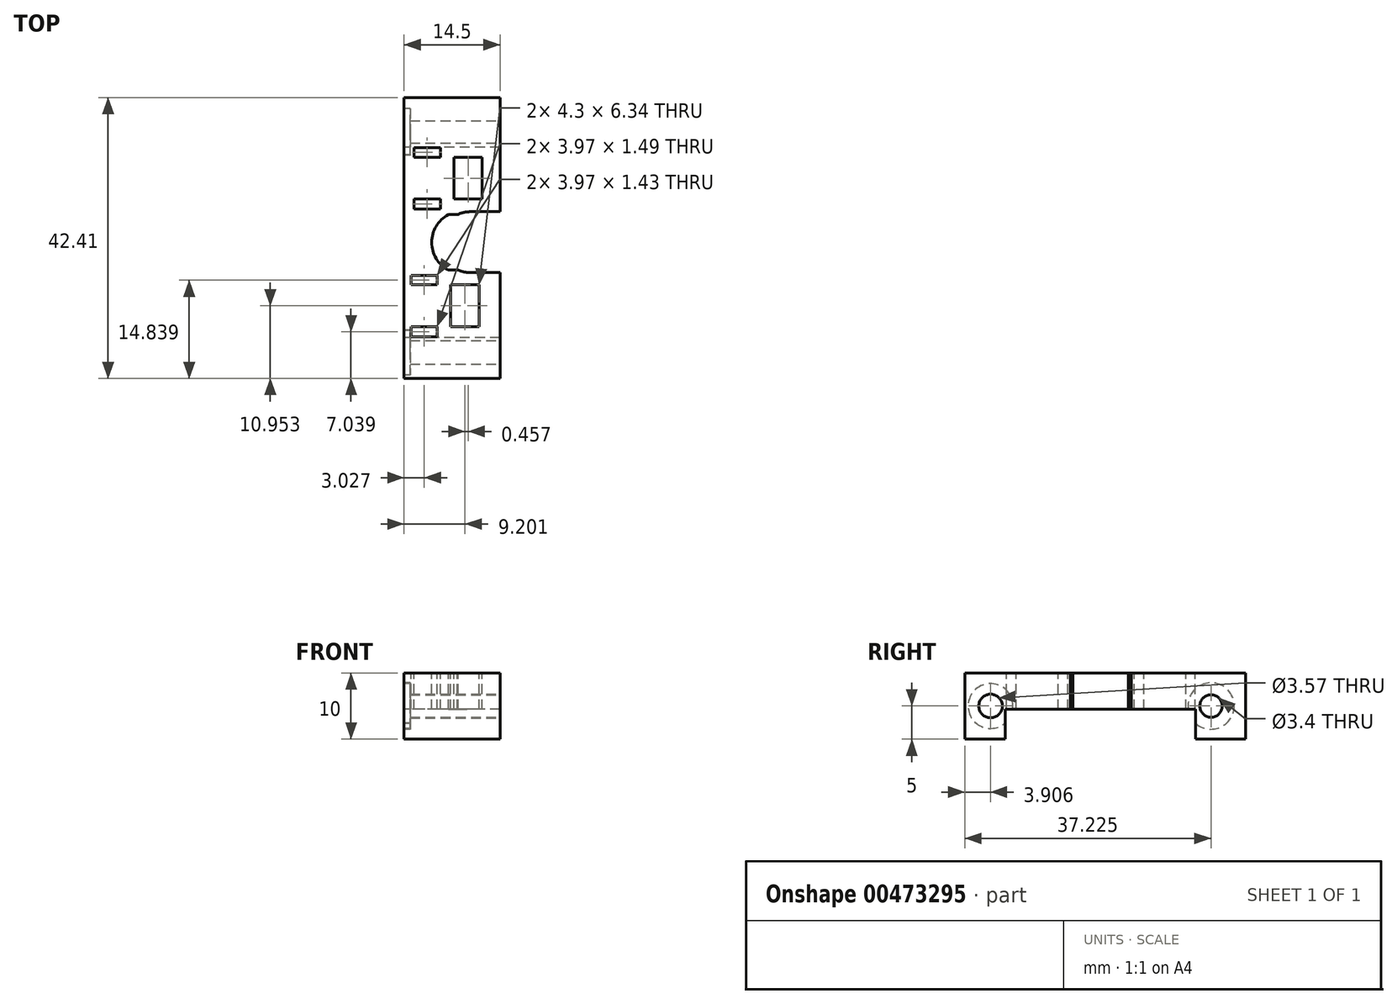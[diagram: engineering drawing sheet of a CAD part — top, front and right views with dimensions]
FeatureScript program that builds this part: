
annotation { "Feature Type Name" : "Feature", "Feature Type Description" : "" }
export const myFeature = defineFeature(function(context is Context, id is Id, definition is map)
    precondition{}
    {
        {
            var Q0;
            Q0=qCreatedBy(makeId("Top.planeOp"),FACE);
            var sketch = newSketch(context, id + "F0", { "sketchPlane" : qUnion([Q0])});
            skLineSegment(sketch, "E0.bottom", {"start": v(8.3, 21.21) * mm, "end": v(-6.2, 21.21) * mm});
            skLineSegment(sketch, "E0.top", {"start": v(8.3, -21.2) * mm, "end": v(-6.2, -21.2) * mm});
            skLineSegment(sketch, "E0.left", {"start": v(8.3, 21.21) * mm, "end": v(8.3, -21.2) * mm});
            skLineSegment(sketch, "E0.right", {"start": v(-6.2, 21.21) * mm, "end": v(-6.2, 5.08) * mm});
            skPoint(sketch, "E1", {"position": v(-1.7, 3.88) * mm});
            skPoint(sketch, "E2", {"position": v(-1.7, -5.12) * mm});
            skLineSegment(sketch, "E3.trimOffspring", {"start": v(-6.2, -6.32) * mm, "end": v(-6.2, -21.2) * mm});
            skCircle(sketch, "E4.0", {"center": v(5.4, -9.25) * mm, "radius": 1.75 * mm});
            skLineSegment(sketch, "E5.0", {"start": v(-1.7, 5.08) * mm, "end": v(-6.2, 5.08) * mm});
            skArc(sketch, "E5.1", {"start": v(-1.7, -6.32) * mm, "mid": v(4, -0.62) * mm, "end": v(-1.7, 5.08) * mm});
            skLineSegment(sketch, "E5.2", {"start": v(-1.7, -6.32) * mm, "end": v(-6.2, -6.32) * mm});
            skSolve(sketch);
        }
        {
            var Q0;
            Q0 = qSketchRegion(id + "F0", true);
            extrude(context, id + "F1", {"entities" : qUnion([Q0]), "depth" : 10 * mm, "offsetDistance" : 25 * mm});
        }
        {
            var Q0;
            Q0=makeQuery(id+"F1.opExtrude","SWEPT_FACE",FACE,{"disambiguationData":[OSD([sQuery(id+"F0.wireOp",EDGE,"E0.left")])]});
            var sketch = newSketch(context, id + "F2", { "sketchPlane" : qUnion([Q0])});
            skCircle(sketch, "E6.0", {"center": v(-17.3, 5) * mm, "radius": 1.78 * mm});
            skCircle(sketch, "E7.0", {"center": v(16.03, 5) * mm, "radius": 1.7 * mm});
            skPoint(sketch, "E8", {"position": v(-21.2, 5) * mm});
            skSolve(sketch);
        }
        {
            var Q0;
            Q0 = qSketchRegion(id + "F2", true);
            extrude(context, id + "F3", {"entities" : qUnion([Q0]), "operationType" : NewBodyOperationType.REMOVE, "oppositeDirection" : true, "depth" : 25 * mm, "offsetDistance" : 25 * mm});
        }
        {
            var Q0;
            Q0=makeQuery(id+"F1.opExtrude","SWEPT_BODY",BODY,{"disambiguationData":[OSD([sQuery(id+"F0.wireOp",EDGE,"E0.bottom"),sQuery(id+"F0.wireOp",EDGE,"E0.top"),sQuery(id+"F0.wireOp",EDGE,"E0.left"),sQuery(id+"F0.wireOp",EDGE,"E0.right"),sQuery(id+"F0.wireOp",EDGE,"E3.trimOffspring"),sQuery(id+"F0.wireOp",EDGE,"E4.0"),sQuery(id+"F0.wireOp",EDGE,"E5.0"),sQuery(id+"F0.wireOp",EDGE,"E5.1"),sQuery(id+"F0.wireOp",EDGE,"E5.2")])]});
            var Q1;
            Q1=makeQuery(id+"F1.opExtrude","SWEPT_FACE",FACE,{"disambiguationData":[OSD([sQuery(id+"F0.wireOp",EDGE,"E0.right")])]});
            mirror(context, id + "F4", {"operationType" : NewBodyOperationType.ADD, "entities" : qUnion([Q0]), "mirrorPlane" : qUnion([Q1])});
        }
        {
            var Q0;
            {var subQ0=makeQuery(id+"F1.opExtrude","CAP_FACE",FACE,{"disambiguationData":[OSD([sQuery(id+"F0.wireOp",EDGE,"E0.bottom"),sQuery(id+"F0.wireOp",EDGE,"E0.top"),sQuery(id+"F0.wireOp",EDGE,"E0.left"),sQuery(id+"F0.wireOp",EDGE,"E0.right"),sQuery(id+"F0.wireOp",EDGE,"E3.trimOffspring"),sQuery(id+"F0.wireOp",EDGE,"E4.0"),sQuery(id+"F0.wireOp",EDGE,"E5.0"),sQuery(id+"F0.wireOp",EDGE,"E5.1"),sQuery(id+"F0.wireOp",EDGE,"E5.2")])],"isStart":false});Q0=makeQuery(id+"F4.boolean.opBoolean","MERGE",FACE,{"derivedFrom":[subQ0,makeQuery(id+"F4.opPattern","COPY",FACE,{"derivedFrom":subQ0,"instanceName":"1"})]});}
            var sketch = newSketch(context, id + "F5", { "sketchPlane" : qUnion([Q0])});
            skLineSegment(sketch, "E9.bottom", {"start": v(-6.2, -21.2) * mm, "end": v(17.5, -21.2) * mm});
            skLineSegment(sketch, "E9.top", {"start": v(-6.2, 26.64) * mm, "end": v(17.5, 26.64) * mm});
            skLineSegment(sketch, "E9.left", {"start": v(-6.2, -21.2) * mm, "end": v(-6.2, 26.64) * mm});
            skLineSegment(sketch, "E9.right", {"start": v(17.5, -21.2) * mm, "end": v(17.5, 26.64) * mm});
            skSolve(sketch);
        }
        {
            var Q0;
            Q0 = qSketchRegion(id + "F5", true);
            extrude(context, id + "F6", {"entities" : qUnion([Q0]), "operationType" : NewBodyOperationType.REMOVE, "oppositeDirection" : true, "depth" : 25 * mm, "offsetDistance" : 25 * mm});
        }
        {
            var Q0;
            {var subQ0=makeQuery(id+"F1.opExtrude","CAP_FACE",FACE,{"disambiguationData":[OSD([sQuery(id+"F0.wireOp",EDGE,"E0.bottom"),sQuery(id+"F0.wireOp",EDGE,"E0.top"),sQuery(id+"F0.wireOp",EDGE,"E0.left"),sQuery(id+"F0.wireOp",EDGE,"E0.right"),sQuery(id+"F0.wireOp",EDGE,"E3.trimOffspring"),sQuery(id+"F0.wireOp",EDGE,"E4.0"),sQuery(id+"F0.wireOp",EDGE,"E5.0"),sQuery(id+"F0.wireOp",EDGE,"E5.1"),sQuery(id+"F0.wireOp",EDGE,"E5.2")])],"isStart":false});Q0=makeQuery(id+"F4.boolean.opBoolean","MERGE",FACE,{"derivedFrom":[subQ0,makeQuery(id+"F4.opPattern","COPY",FACE,{"derivedFrom":subQ0,"instanceName":"1"})]});}
            var sketch = newSketch(context, id + "F7", { "sketchPlane" : qUnion([Q0])});
            skCircle(sketch, "E10.0", {"center": v(-17.8, -9.25) * mm, "radius": 1.75 * mm});
            skSolve(sketch);
        }
        {
            var Q0;
            Q0 = qSketchRegion(id + "F7", true);
            var Q1;
            {var subQ0=makeQuery(id+"F1.opExtrude","CAP_FACE",FACE,{"disambiguationData":[OSD([sQuery(id+"F0.wireOp",EDGE,"E0.bottom"),sQuery(id+"F0.wireOp",EDGE,"E0.top"),sQuery(id+"F0.wireOp",EDGE,"E0.left"),sQuery(id+"F0.wireOp",EDGE,"E0.right"),sQuery(id+"F0.wireOp",EDGE,"E3.trimOffspring"),sQuery(id+"F0.wireOp",EDGE,"E4.0"),sQuery(id+"F0.wireOp",EDGE,"E5.0"),sQuery(id+"F0.wireOp",EDGE,"E5.1"),sQuery(id+"F0.wireOp",EDGE,"E5.2")])],"isStart":true});Q1=makeQuery(id+"F4.boolean.opBoolean","MERGE",FACE,{"derivedFrom":[subQ0,makeQuery(id+"F4.opPattern","COPY",FACE,{"derivedFrom":subQ0,"instanceName":"1"})]});}
            extrude(context, id + "F8", {"entities" : qUnion([Q0]), "operationType" : NewBodyOperationType.ADD, "endBound" : BoundingType.UP_TO_SURFACE, "oppositeDirection" : true, "depth" : 25 * mm, "endBoundEntityFace" : qUnion([Q1]), "offsetDistance" : 25 * mm});
        }
        {
            var Q0;
            {var subQ0=makeQuery(id+"F1.opExtrude","CAP_FACE",FACE,{"disambiguationData":[OSD([sQuery(id+"F0.wireOp",EDGE,"E0.bottom"),sQuery(id+"F0.wireOp",EDGE,"E0.top"),sQuery(id+"F0.wireOp",EDGE,"E0.left"),sQuery(id+"F0.wireOp",EDGE,"E0.right"),sQuery(id+"F0.wireOp",EDGE,"E3.trimOffspring"),sQuery(id+"F0.wireOp",EDGE,"E4.0"),sQuery(id+"F0.wireOp",EDGE,"E5.0"),sQuery(id+"F0.wireOp",EDGE,"E5.1"),sQuery(id+"F0.wireOp",EDGE,"E5.2")])],"isStart":false});Q0=makeQuery(id+"F8.boolean.opBoolean","MERGE",FACE,{"derivedFrom":[makeQuery(id+"F4.boolean.opBoolean","MERGE",FACE,{"derivedFrom":[subQ0,makeQuery(id+"F4.opPattern","COPY",FACE,{"derivedFrom":subQ0,"instanceName":"1"})]}),makeQuery(id+"F8.opExtrude","CAP_FACE",FACE,{"disambiguationData":[OSD([sQuery(id+"F7.wireOp",EDGE,"E10.0")])],"isStart":true})]});}
            var sketch = newSketch(context, id + "F9", { "sketchPlane" : qUnion([Q0])});
            skLineSegment(sketch, "E11", {"start": v(-20.7, 0) * mm, "end": v(-3.31, 0) * mm, "construction": true});
            skLineSegment(sketch, "E12.bottom", {"start": v(-9.35, -7.08) * mm, "end": v(-13.65, -7.08) * mm});
            skLineSegment(sketch, "E12.top", {"start": v(-9.35, -13.42) * mm, "end": v(-13.65, -13.42) * mm});
            skLineSegment(sketch, "E12.left", {"start": v(-9.35, -7.08) * mm, "end": v(-9.35, -13.42) * mm});
            skLineSegment(sketch, "E12.right", {"start": v(-13.65, -7.08) * mm, "end": v(-13.65, -13.42) * mm});
            skLineSegment(sketch, "E13.bottom", {"start": v(-15.69, -7.08) * mm, "end": v(-19.66, -7.08) * mm});
            skLineSegment(sketch, "E13.top", {"start": v(-15.69, -5.64) * mm, "end": v(-19.66, -5.64) * mm});
            skLineSegment(sketch, "E13.left", {"start": v(-15.69, -7.08) * mm, "end": v(-15.69, -5.64) * mm});
            skLineSegment(sketch, "E13.right", {"start": v(-19.66, -7.08) * mm, "end": v(-19.66, -5.64) * mm});
            skLineSegment(sketch, "E14.bottom", {"start": v(-15.69, -13.42) * mm, "end": v(-19.66, -13.42) * mm});
            skLineSegment(sketch, "E14.top", {"start": v(-15.69, -14.9) * mm, "end": v(-19.66, -14.9) * mm});
            skLineSegment(sketch, "E14.left", {"start": v(-15.69, -13.42) * mm, "end": v(-15.69, -14.9) * mm});
            skLineSegment(sketch, "E14.right", {"start": v(-19.66, -13.42) * mm, "end": v(-19.66, -14.9) * mm});
            skLineSegment(sketch, "E15.bottom", {"start": v(-8.9, 12.22) * mm, "end": v(-13.2, 12.22) * mm});
            skLineSegment(sketch, "E15.top", {"start": v(-8.9, 5.88) * mm, "end": v(-13.2, 5.88) * mm});
            skLineSegment(sketch, "E15.left", {"start": v(-8.9, 12.22) * mm, "end": v(-8.9, 5.88) * mm});
            skLineSegment(sketch, "E15.right", {"start": v(-13.2, 12.22) * mm, "end": v(-13.2, 5.88) * mm});
            skLineSegment(sketch, "E16.bottom", {"start": v(-15.23, 12.22) * mm, "end": v(-19.2, 12.22) * mm});
            skLineSegment(sketch, "E16.top", {"start": v(-15.23, 13.65) * mm, "end": v(-19.2, 13.65) * mm});
            skLineSegment(sketch, "E16.left", {"start": v(-15.23, 12.22) * mm, "end": v(-15.23, 13.65) * mm});
            skLineSegment(sketch, "E16.right", {"start": v(-19.2, 12.22) * mm, "end": v(-19.2, 13.65) * mm});
            skLineSegment(sketch, "E17.bottom", {"start": v(-15.23, 5.88) * mm, "end": v(-19.2, 5.88) * mm});
            skLineSegment(sketch, "E17.top", {"start": v(-15.23, 4.4) * mm, "end": v(-19.2, 4.4) * mm});
            skLineSegment(sketch, "E17.left", {"start": v(-15.23, 5.88) * mm, "end": v(-15.23, 4.4) * mm});
            skLineSegment(sketch, "E17.right", {"start": v(-19.2, 5.88) * mm, "end": v(-19.2, 4.4) * mm});
            skSolve(sketch);
        }
        {
            var Q0;
            Q0 = qSketchRegion(id + "F9", true);
            extrude(context, id + "F10", {"entities" : qUnion([Q0]), "operationType" : NewBodyOperationType.REMOVE, "oppositeDirection" : true, "depth" : 25 * mm, "offsetDistance" : 25 * mm});
        }
        {
            var Q0;
            {var subQ0=makeQuery(id+"F1.opExtrude","CAP_FACE",FACE,{"disambiguationData":[OSD([sQuery(id+"F0.wireOp",EDGE,"E0.bottom"),sQuery(id+"F0.wireOp",EDGE,"E0.top"),sQuery(id+"F0.wireOp",EDGE,"E0.left"),sQuery(id+"F0.wireOp",EDGE,"E0.right"),sQuery(id+"F0.wireOp",EDGE,"E3.trimOffspring"),sQuery(id+"F0.wireOp",EDGE,"E4.0"),sQuery(id+"F0.wireOp",EDGE,"E5.0"),sQuery(id+"F0.wireOp",EDGE,"E5.1"),sQuery(id+"F0.wireOp",EDGE,"E5.2")])],"isStart":false});Q0=makeQuery(id+"F8.boolean.opBoolean","MERGE",FACE,{"derivedFrom":[makeQuery(id+"F4.boolean.opBoolean","MERGE",FACE,{"derivedFrom":[subQ0,makeQuery(id+"F4.opPattern","COPY",FACE,{"derivedFrom":subQ0,"instanceName":"1"})]}),makeQuery(id+"F8.opExtrude","CAP_FACE",FACE,{"disambiguationData":[OSD([sQuery(id+"F7.wireOp",EDGE,"E10.0")])],"isStart":true})]});}
            var sketch = newSketch(context, id + "F11", { "sketchPlane" : qUnion([Q0])});
            skLineSegment(sketch, "E18.0", {"start": v(-6.2, 3.98) * mm, "end": v(-10.7, 3.98) * mm});
            skArc(sketch, "E18.1", {"start": v(-10.7, -5.22) * mm, "mid": v(-15.3, -0.62) * mm, "end": v(-10.7, 3.98) * mm});
            skLineSegment(sketch, "E18.2", {"start": v(-6.2, -5.22) * mm, "end": v(-10.7, -5.22) * mm});
            skLineSegment(sketch, "E19", {"start": v(-6.2, 3.98) * mm, "end": v(-6.2, 5.08) * mm});
            skLineSegment(sketch, "E20", {"start": v(-6.2, -6.32) * mm, "end": v(-6.2, -5.22) * mm});
            skArc(sketch, "E21.0", {"start": v(-10.7, -6.32) * mm, "mid": v(-16.4, -0.62) * mm, "end": v(-10.7, 5.08) * mm});
            skLineSegment(sketch, "E22.0", {"start": v(-6.2, 5.08) * mm, "end": v(-10.7, 5.08) * mm});
            skLineSegment(sketch, "E23.0", {"start": v(-6.2, -6.32) * mm, "end": v(-10.7, -6.32) * mm});
            skSolve(sketch);
        }
        {
            var Q0;
            Q0 = qSketchRegion(id + "F11", true);
            var Q1;
            {var subQ0=makeQuery(id+"F1.opExtrude","CAP_FACE",FACE,{"disambiguationData":[OSD([sQuery(id+"F0.wireOp",EDGE,"E0.bottom"),sQuery(id+"F0.wireOp",EDGE,"E0.top"),sQuery(id+"F0.wireOp",EDGE,"E0.left"),sQuery(id+"F0.wireOp",EDGE,"E0.right"),sQuery(id+"F0.wireOp",EDGE,"E3.trimOffspring"),sQuery(id+"F0.wireOp",EDGE,"E4.0"),sQuery(id+"F0.wireOp",EDGE,"E5.0"),sQuery(id+"F0.wireOp",EDGE,"E5.1"),sQuery(id+"F0.wireOp",EDGE,"E5.2")])],"isStart":true});Q1=makeQuery(id+"F8.boolean.opBoolean","MERGE",FACE,{"derivedFrom":[makeQuery(id+"F4.boolean.opBoolean","MERGE",FACE,{"derivedFrom":[subQ0,makeQuery(id+"F4.opPattern","COPY",FACE,{"derivedFrom":subQ0,"instanceName":"1"})]}),makeQuery(id+"F8.opExtrude","CAP_FACE",FACE,{"disambiguationData":[OSD([sQuery(id+"F7.wireOp",EDGE,"E10.0")])],"isStart":false})]});}
            extrude(context, id + "F12", {"entities" : qUnion([Q0]), "operationType" : NewBodyOperationType.ADD, "endBound" : BoundingType.UP_TO_SURFACE, "oppositeDirection" : true, "depth" : 25 * mm, "endBoundEntityFace" : qUnion([Q1]), "offsetDistance" : 25 * mm});
        }
        {
            var Q0;
            Q0=makeQuery(id+"F4.opPattern","COPY",FACE,{"derivedFrom":makeQuery(id+"F1.opExtrude","SWEPT_FACE",FACE,{"disambiguationData":[OSD([sQuery(id+"F0.wireOp",EDGE,"E0.left")])]}),"instanceName":"1"});
            var sketch = newSketch(context, id + "F13", { "sketchPlane" : qUnion([Q0])});
            skLineSegment(sketch, "E24.bottom", {"start": v(-13.7, 0) * mm, "end": v(15.08, 0) * mm});
            skLineSegment(sketch, "E24.top", {"start": v(-13.7, 4.5) * mm, "end": v(15.08, 4.5) * mm});
            skLineSegment(sketch, "E24.left", {"start": v(-13.7, 0) * mm, "end": v(-13.7, 4.5) * mm});
            skLineSegment(sketch, "E24.right", {"start": v(15.08, 0) * mm, "end": v(15.08, 4.5) * mm});
            skSolve(sketch);
        }
        {
            var Q0;
            Q0 = qSketchRegion(id + "F13", true);
            extrude(context, id + "F14", {"entities" : qUnion([Q0]), "operationType" : NewBodyOperationType.REMOVE, "oppositeDirection" : true, "depth" : 25 * mm, "offsetDistance" : 25 * mm});
        }
        {
            var Q0;
            {var subQ0=makeQuery(id+"F1.opExtrude","CAP_FACE",FACE,{"disambiguationData":[OSD([sQuery(id+"F0.wireOp",EDGE,"E0.bottom"),sQuery(id+"F0.wireOp",EDGE,"E0.top"),sQuery(id+"F0.wireOp",EDGE,"E0.left"),sQuery(id+"F0.wireOp",EDGE,"E0.right"),sQuery(id+"F0.wireOp",EDGE,"E3.trimOffspring"),sQuery(id+"F0.wireOp",EDGE,"E4.0"),sQuery(id+"F0.wireOp",EDGE,"E5.0"),sQuery(id+"F0.wireOp",EDGE,"E5.1"),sQuery(id+"F0.wireOp",EDGE,"E5.2")])],"isStart":false});Q0=makeQuery(id+"F12.boolean.opBoolean","MERGE",FACE,{"derivedFrom":[makeQuery(id+"F8.boolean.opBoolean","MERGE",FACE,{"derivedFrom":[makeQuery(id+"F4.boolean.opBoolean","MERGE",FACE,{"derivedFrom":[subQ0,makeQuery(id+"F4.opPattern","COPY",FACE,{"derivedFrom":subQ0,"instanceName":"1"})]}),makeQuery(id+"F8.opExtrude","CAP_FACE",FACE,{"disambiguationData":[OSD([sQuery(id+"F7.wireOp",EDGE,"E10.0")])],"isStart":true})]}),makeQuery(id+"F12.opExtrude","CAP_FACE",FACE,{"disambiguationData":[OSD([sQuery(id+"F11.wireOp",EDGE,"E18.0"),sQuery(id+"F11.wireOp",EDGE,"E18.1"),sQuery(id+"F11.wireOp",EDGE,"E18.2"),sQuery(id+"F11.wireOp",EDGE,"E19"),sQuery(id+"F11.wireOp",EDGE,"E20"),sQuery(id+"F11.wireOp",EDGE,"E21.0"),sQuery(id+"F11.wireOp",EDGE,"E22.0"),sQuery(id+"F11.wireOp",EDGE,"E23.0")])],"isStart":true})]});}
            var sketch = newSketch(context, id + "F15", { "sketchPlane" : qUnion([Q0])});
            skLineSegment(sketch, "E25", {"start": v(-10.4, -4.84) * mm, "end": v(-14.02, -4.84) * mm});
            skLineSegment(sketch, "E26", {"start": v(-10.4, 3.53) * mm, "end": v(-14.02, 3.53) * mm});
            skArc(sketch, "E27", {"start": v(-14.02, 3.53) * mm, "mid": v(-16.53, -0.65) * mm, "end": v(-14.02, -4.84) * mm});
            skLineSegment(sketch, "E28", {"start": v(-10.4, 3.53) * mm, "end": v(-10.4, -4.84) * mm});
            skSolve(sketch);
        }
        {
            var Q0;
            Q0 = qSketchRegion(id + "F15", true);
            extrude(context, id + "F16", {"entities" : qUnion([Q0]), "operationType" : NewBodyOperationType.REMOVE, "oppositeDirection" : true, "depth" : 25 * mm, "offsetDistance" : 25 * mm});
        }
        {
            var Q0;
            Q0=makeQuery(id+"F4.opPattern","COPY",FACE,{"derivedFrom":makeQuery(id+"F1.opExtrude","SWEPT_FACE",FACE,{"disambiguationData":[OSD([sQuery(id+"F0.wireOp",EDGE,"E0.left")])]}),"instanceName":"1"});
            var sketch = newSketch(context, id + "F17", { "sketchPlane" : qUnion([Q0])});
            skCircle(sketch, "E29", {"center": v(-16.03, 5) * mm, "radius": 3.5 * mm});
            skCircle(sketch, "E30", {"center": v(17.3, 5) * mm, "radius": 3.39 * mm});
            skSolve(sketch);
        }
        {
            var Q0;
            Q0 = qSketchRegion(id + "F17", true);
            extrude(context, id + "F18", {"entities" : qUnion([Q0]), "operationType" : NewBodyOperationType.REMOVE, "oppositeDirection" : true, "depth" : 0.9 * mm, "offsetDistance" : 25 * mm});
        }
    });
